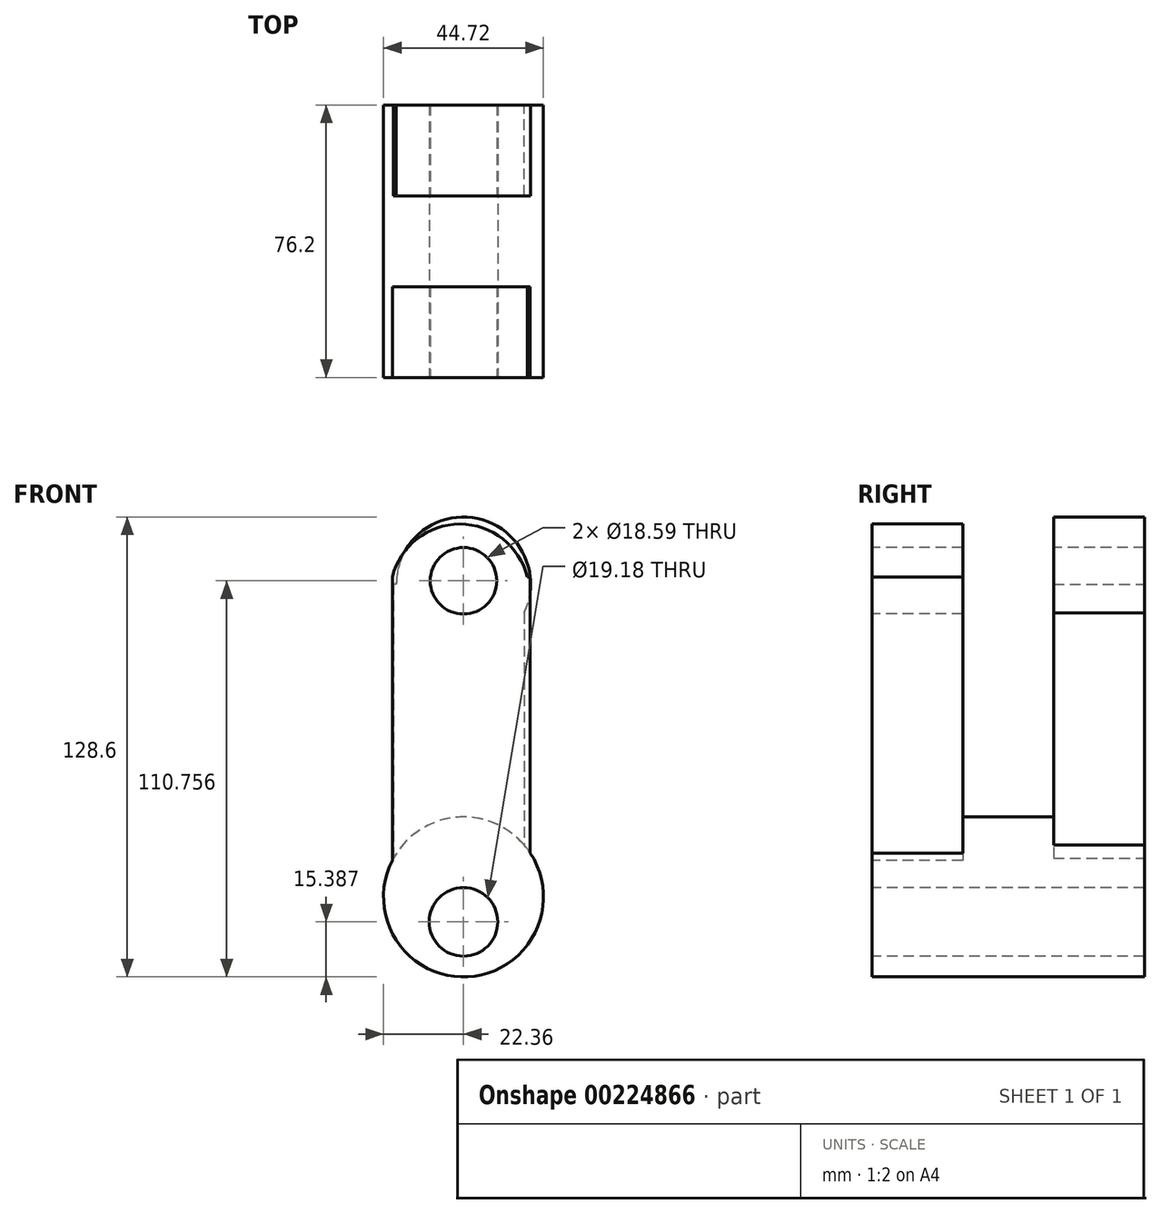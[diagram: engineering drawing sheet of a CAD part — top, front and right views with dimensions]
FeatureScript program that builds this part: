
annotation { "Feature Type Name" : "Feature", "Feature Type Description" : "" }
export const myFeature = defineFeature(function(context is Context, id is Id, definition is map)
    precondition{}
    {
        {
            var Q0;
            Q0=qCreatedBy(makeId("Front.planeOp"),FACE);
            var sketch = newSketch(context, id + "F0", { "sketchPlane" : qUnion([Q0])});
            skCircle(sketch, "E0", {"center": v(0, -38.82) * mm, "radius": 22.36 * mm});
            skSolve(sketch);
        }
        {
            var Q0;
            Q0=makeQuery(id+"F0.imprint","IMPRINT",FACE,{"disambiguationData":[TD([[makeQuery(id+"F0.imprint","IMPRINT",EDGE,{"derivedFrom":sQuery(id+"F0.wireOp",EDGE,"E0")}),1.0]])]});
            extrude(context, id + "F10", {"entities" : qUnion([Q0]), "depth" : 25.4 * mm});
        }
        {
            var Q0;
            Q0=makeQuery(id+"F10.opExtrude","CAP_FACE",FACE,{"disambiguationData":[OSD([sQuery(id+"F0.wireOp",EDGE,"E0")])],"isStart":false});
            extrude(context, id + "F1", {"entities" : qUnion([Q0]), "operationType" : NewBodyOperationType.ADD, "depth" : 50.8 * mm});
        }
        {
            var Q0;
            Q0=makeQuery(id+"F1.opExtrude","CAP_FACE",FACE,{"disambiguationData":[OSD([sQuery(id+"F0.wireOp",EDGE,"E0")])],"isStart":false});
            var sketch = newSketch(context, id + "F2", { "sketchPlane" : qUnion([Q0])});
            skLineSegment(sketch, "E1.bottom", {"start": v(18.69, 50.66) * mm, "end": v(-19.9, 50.66) * mm});
            skLineSegment(sketch, "E1.top", {"start": v(18.69, -28.61) * mm, "end": v(-19.9, -28.61) * mm});
            skLineSegment(sketch, "E1.left", {"start": v(18.69, 50.66) * mm, "end": v(18.69, -28.61) * mm});
            skLineSegment(sketch, "E1.right", {"start": v(-19.9, 50.66) * mm, "end": v(-19.9, -28.61) * mm});
            skSolve(sketch);
        }
        {
            var Q0;
            {var subQ0=sQuery(id+"F2.wireOp",EDGE,"E1.bottom");Q0=makeQuery(id+"F2.imprint","IMPRINT",FACE,{"disambiguationData":[TD([[makeQuery(id+"F2.imprint","IMPRINT",EDGE,{"derivedFrom":subQ0}),1.0]])]});}
            extrude(context, id + "F11", {"entities" : qUnion([Q0]), "operationType" : NewBodyOperationType.ADD, "oppositeDirection" : true, "depth" : 25.4 * mm});
        }
        {
            var Q0;
            Q0=makeQuery(id+"F10.opExtrude","CAP_FACE",FACE,{"disambiguationData":[OSD([sQuery(id+"F0.wireOp",EDGE,"E0")])],"isStart":true});
            var sketch = newSketch(context, id + "F12", { "sketchPlane" : qUnion([Q0])});
            skLineSegment(sketch, "E2.bottom", {"start": v(-16.94, 48.66) * mm, "end": v(19.57, 48.66) * mm});
            skLineSegment(sketch, "E2.top", {"start": v(-16.94, -28.02) * mm, "end": v(19.57, -28.02) * mm});
            skLineSegment(sketch, "E2.left", {"start": v(-16.94, 48.66) * mm, "end": v(-16.94, -28.02) * mm});
            skLineSegment(sketch, "E2.right", {"start": v(19.57, 48.66) * mm, "end": v(19.57, -28.02) * mm});
            skSolve(sketch);
        }
        {
            var Q0;
            {var subQ0=sQuery(id+"F12.wireOp",EDGE,"E2.bottom");Q0=makeQuery(id+"F12.imprint","IMPRINT",FACE,{"disambiguationData":[TD([[makeQuery(id+"F12.imprint","IMPRINT",EDGE,{"derivedFrom":subQ0}),-1.0]])]});}
            extrude(context, id + "F3", {"entities" : qUnion([Q0]), "operationType" : NewBodyOperationType.ADD, "oppositeDirection" : true, "depth" : 25.4 * mm});
        }
        {
            var Q0;
            {var subQ0=sQuery(id+"F0.wireOp",EDGE,"E0");Q0=makeQuery(id+"F11.boolean.opBoolean","MERGE",FACE,{"derivedFrom":[makeQuery(id+"F1.opExtrude","CAP_FACE",FACE,{"disambiguationData":[OSD([subQ0])],"isStart":false}),makeQuery(id+"F11.opExtrude","CAP_FACE",FACE,{"disambiguationData":[OSD([subQ0,sQuery(id+"F2.wireOp",EDGE,"E1.bottom"),sQuery(id+"F2.wireOp",EDGE,"E1.left"),sQuery(id+"F2.wireOp",EDGE,"E1.right")])],"isStart":true})]});}
            var sketch = newSketch(context, id + "F13", { "sketchPlane" : qUnion([Q0])});
            skArc(sketch, "E3", {"start": v(18.16, 49.1) * mm, "mid": v(-0.23, 65.43) * mm, "end": v(-19.9, 50.66) * mm});
            skSolve(sketch);
        }
        {
            var Q0;
            {var subQ0=sQuery(id+"F13.wireOp",EDGE,"E3");var subQ1=makeQuery(id+"F11.opExtrude","CAP_EDGE",EDGE,{"disambiguationData":[OSD([sQuery(id+"F2.wireOp",EDGE,"E1.bottom")])],"isStart":true});var subQ3=makeQuery(id+"F13.imprint","INTERSECT",VERTEX,{"derivedFrom":[subQ1,subQ0]});Q0=makeQuery(id+"F13.imprint","IMPRINT",FACE,{"disambiguationData":[TD([[makeQuery(id+"F13.imprint","IMPRINT",EDGE,{"disambiguationData":[TD([[subQ3,-1.0]])],"derivedFrom":subQ0}),1.0]])]});}
            extrude(context, id + "F14", {"entities" : qUnion([Q0]), "operationType" : NewBodyOperationType.ADD, "oppositeDirection" : true, "depth" : 25.4 * mm});
        }
        {
            var Q0;
            {var subQ0=sQuery(id+"F0.wireOp",EDGE,"E0");Q0=makeQuery(id+"F3.boolean.opBoolean","MERGE",FACE,{"derivedFrom":[makeQuery(id+"F10.opExtrude","CAP_FACE",FACE,{"disambiguationData":[OSD([subQ0])],"isStart":true}),makeQuery(id+"F3.opExtrude","CAP_FACE",FACE,{"disambiguationData":[OSD([subQ0,sQuery(id+"F12.wireOp",EDGE,"E2.bottom"),sQuery(id+"F12.wireOp",EDGE,"E2.left"),sQuery(id+"F12.wireOp",EDGE,"E2.right")])],"isStart":true})]});}
            var sketch = newSketch(context, id + "F4", { "sketchPlane" : qUnion([Q0])});
            skCircle(sketch, "E4", {"center": v(0, 48.66) * mm, "radius": 18.77 * mm});
            skPoint(sketch, "E4.centerSnap0", {"position": v(1.31, 48.66) * mm});
            skSolve(sketch);
        }
        {
            var Q0;
            {var subQ0=sQuery(id+"F4.wireOp",EDGE,"E4");var subQ1=makeQuery(id+"F3.opExtrude","CAP_EDGE",EDGE,{"disambiguationData":[OSD([sQuery(id+"F12.wireOp",EDGE,"E2.bottom")])],"isStart":true});var subQ2=makeQuery(id+"F4.imprint","INTERSECT",VERTEX,{"derivedFrom":[subQ1,subQ0]});Q0=makeQuery(id+"F4.imprint","IMPRINT",FACE,{"disambiguationData":[TD([[makeQuery(id+"F4.imprint","IMPRINT",EDGE,{"disambiguationData":[TD([[subQ2,-1.0]])],"derivedFrom":subQ0}),1.0]])]});}
            extrude(context, id + "F5", {"entities" : qUnion([Q0]), "operationType" : NewBodyOperationType.ADD, "oppositeDirection" : true, "depth" : 25.4 * mm});
        }
        {
            var Q0;
            {var subQ0=sQuery(id+"F2.wireOp",EDGE,"E1.bottom");var subQ1=sQuery(id+"F0.wireOp",EDGE,"E0");Q0=makeQuery(id+"F14.boolean.opBoolean","MERGE",FACE,{"derivedFrom":[makeQuery(id+"F11.boolean.opBoolean","MERGE",FACE,{"derivedFrom":[makeQuery(id+"F1.opExtrude","CAP_FACE",FACE,{"disambiguationData":[OSD([subQ1])],"isStart":false}),makeQuery(id+"F11.opExtrude","CAP_FACE",FACE,{"disambiguationData":[OSD([subQ1,subQ0,sQuery(id+"F2.wireOp",EDGE,"E1.left"),sQuery(id+"F2.wireOp",EDGE,"E1.right")])],"isStart":true})]}),makeQuery(id+"F14.opExtrude","CAP_FACE",FACE,{"disambiguationData":[OSD([subQ0,sQuery(id+"F13.wireOp",EDGE,"E3")])],"isStart":true})]});}
            var sketch = newSketch(context, id + "F6", { "sketchPlane" : qUnion([Q0])});
            skCircle(sketch, "E5", {"center": v(0, 49.59) * mm, "radius": 9.3 * mm});
            skSolve(sketch);
        }
        {
            var Q0;
            Q0=makeQuery(id+"F6.imprint","IMPRINT",FACE,{"disambiguationData":[TD([[makeQuery(id+"F6.imprint","IMPRINT",EDGE,{"derivedFrom":sQuery(id+"F6.wireOp",EDGE,"E5")}),1.0]])]});
            var Q1;
            Q1=sQuery(id+"F6.wireOp",EDGE,"E5");
            extrude(context, id + "F7", {"entities" : qUnion([Q0]), "operationType" : NewBodyOperationType.REMOVE, "surfaceEntities" : qUnion([Q1]), "endBound" : BoundingType.THROUGH_ALL, "oppositeDirection" : true, "depth" : 25.4 * mm});
        }
        {
            var Q0;
            {var subQ0=sQuery(id+"F2.wireOp",EDGE,"E1.bottom");var subQ1=sQuery(id+"F0.wireOp",EDGE,"E0");Q0=makeQuery(id+"F14.boolean.opBoolean","MERGE",FACE,{"derivedFrom":[makeQuery(id+"F11.boolean.opBoolean","MERGE",FACE,{"derivedFrom":[makeQuery(id+"F1.opExtrude","CAP_FACE",FACE,{"disambiguationData":[OSD([subQ1])],"isStart":false}),makeQuery(id+"F11.opExtrude","CAP_FACE",FACE,{"disambiguationData":[OSD([subQ1,subQ0,sQuery(id+"F2.wireOp",EDGE,"E1.left"),sQuery(id+"F2.wireOp",EDGE,"E1.right")])],"isStart":true})]}),makeQuery(id+"F14.opExtrude","CAP_FACE",FACE,{"disambiguationData":[OSD([subQ0,sQuery(id+"F13.wireOp",EDGE,"E3")])],"isStart":true})]});}
            var sketch = newSketch(context, id + "F8", { "sketchPlane" : qUnion([Q0])});
            skCircle(sketch, "E6", {"center": v(0, -45.78) * mm, "radius": 9.59 * mm});
            skSolve(sketch);
        }
        {
            var Q0;
            Q0=makeQuery(id+"F8.imprint","IMPRINT",FACE,{"disambiguationData":[TD([[makeQuery(id+"F8.imprint","IMPRINT",EDGE,{"derivedFrom":sQuery(id+"F8.wireOp",EDGE,"E6")}),1.0]])]});
            var Q1;
            Q1=sQuery(id+"F8.wireOp",EDGE,"E6");
            extrude(context, id + "F9", {"entities" : qUnion([Q0]), "operationType" : NewBodyOperationType.REMOVE, "surfaceEntities" : qUnion([Q1]), "endBound" : BoundingType.THROUGH_ALL, "oppositeDirection" : true, "depth" : 25.4 * mm});
        }
    });
